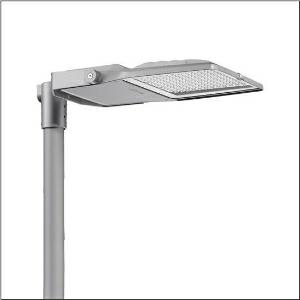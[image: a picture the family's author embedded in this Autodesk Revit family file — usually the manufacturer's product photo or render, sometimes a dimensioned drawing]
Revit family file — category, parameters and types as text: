
# Revit family: floodlight_fl_21_midi___pl43_5xa7786e4a3a_aacc
name_source: partatom
category: Lighting Fixtures
units: mm (PartAtom-declared; Revit-internal decimal feet)

## family parameters
Cut with Voids When Loaded = No
Host = Face
Light Source = No
Part Type = Normal
Room Calculation Point = No
Round Connector Dimension = Use Diameter
Shared = No

## types (1)
- --- (1 x LED, 28830 lm, 212.4 W, 4000K)
    Apparent Load = 212 VA
    CIE Flux Codes = 27 78 99 100 100
    Color Rendering = 70
    Color Temperature = 4000K
    Default Elevation = 1800 mm
    Description = Floodlight FL 21 midi, floodlight, primary light control with lens, of PMMA, primary optical cover: protective disc, of toughened safety glass, transparent, light distribution: PL43, light emission: direct distribution, installation type: surface-mounted, LED, High Power LED, rated luminous flux: 28.830lm, luminous efficacy: 136lm/W, light colour: 740, colour temperature: 4000K, control gear: Smart Interface (Zhaga)D4i, control: overheat protection, constant luminous flux control, time-dependent luminous flux control, flexible luminous flux parameterisation, pre-setting: logarithmic dimming characteristic, with terminal, 6-pole, mains connection: 220..240V, AC, 50/60Hz, start of lifetime: 212W, end of service life: 231W, reduction: 95W, mast bracket, of diecast aluminium, powder-coated, SITECO metallic grey (DB 702S), corrosivity category C5 mid according to DIN EN ISO 12944, suitable for swimming pools, chlorine-resistant, sealing non-destructively replaceable, mast bracket, of steel, galvanised, powder-coated, SITECO metallic grey (DB 702S), Smart Interface below and above, protection rating (complete): IP66, insulation class (complete): insulation class II (safety insulation), certification: CE, ENEC, VDE, protection symbol: D, impact resistance: IK08, permissible operating ambient temperature: -40..+40°C, permissible operating ambient temperature for outdoor applications: -40..+50°C, standard: DIN EN 12944, LABS conformity tested according to VDMA 24364:2018-05, packaging unit: 1 piece

Light Distribution: PL43
    Height = 76 mm
    Lamp = 1 x LED
    Lamp Light Flux = 28830 lm
    Lamp Power = 212.4 W
    Lamp count = 1
    Length = 657 mm
    Luminous efficacy = 136 lm/W
    Manufacturer = Siteco
    ModVariant = No
    Model = 5XA7786E4A3A
    Number of Poles = 1
    OnlyDefault = Yes
    Power Factor = 1
    Product Name = Floodlight FL 21 midi | PL43
    Product group = floodlight | pylon annexe
    ProductGroupID = 6201
    Protection Class = Protection class II
    Protection Degree = IP 66
    RLX_Detail_Level = 1
    RLX_Emergency_Light_Flux = 0 lm
    RLX_Emergency_Type = 0
    RLX_Emergency_Type_DB = No
    RlxData = <blob elided: 104541 chars, md5=b426277f>
    Socket = socket
    Standby Power = 0 W
    System Light Flux = 28830 lm
    System Power = 212 W
    Type Comments = factory setting: luminous flux: 100 % | dim-lin: 254 | 710 mA
    Type Image = l_1007123.jpg
    URL = http://relux.com
    VarID = @adj_093031
    Voltage = 0 V
    Weight = 0.00 kg
    Width = 442 mm

## geometry (parser evidence)
native form markers: Blend x4, Sweep x12
no freeform markers — native parametric forms only
